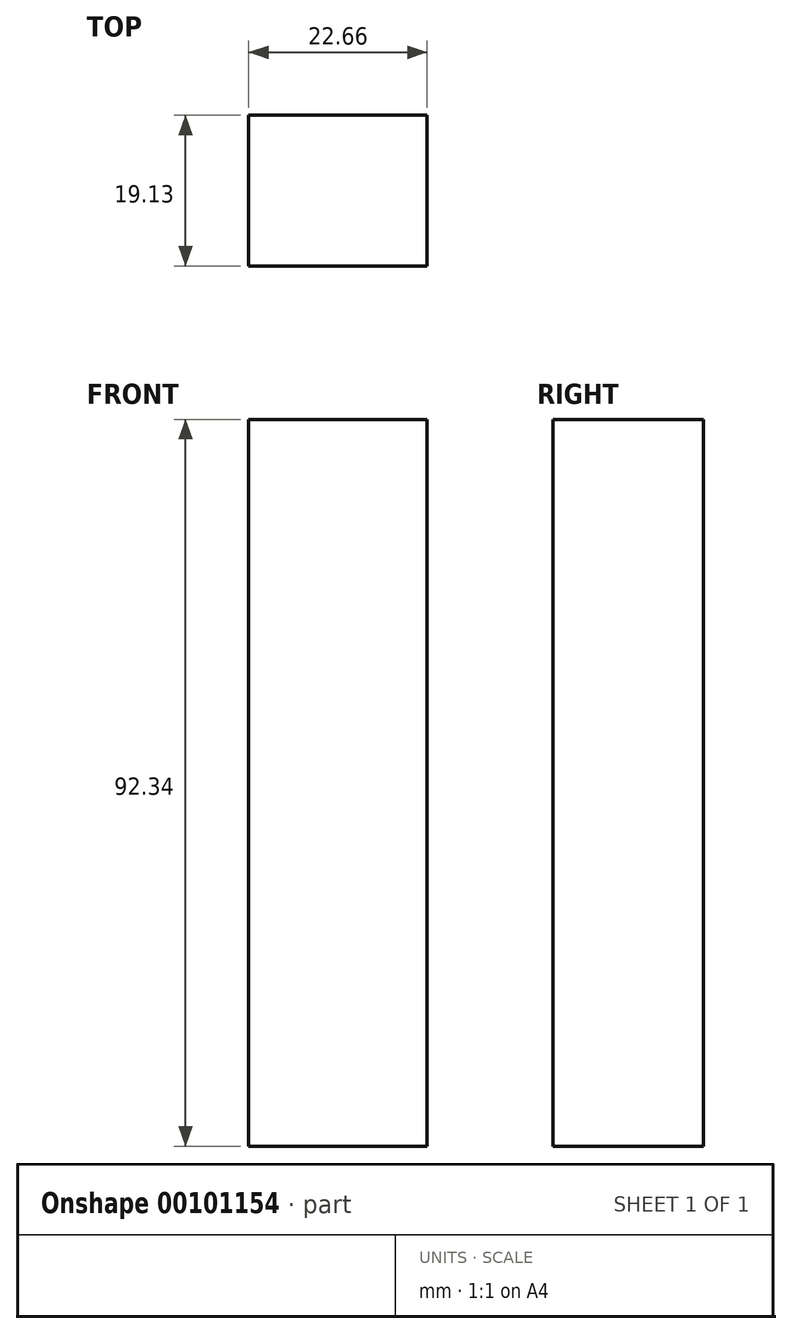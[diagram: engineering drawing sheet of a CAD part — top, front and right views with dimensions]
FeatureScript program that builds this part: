
annotation { "Feature Type Name" : "Feature", "Feature Type Description" : "" }
export const myFeature = defineFeature(function(context is Context, id is Id, definition is map)
    precondition{}
    {
        {
            var Q0;
            Q0=qCreatedBy(makeId("Front.planeOp"),FACE);
            var sketch = newSketch(context, id + "F0", { "sketchPlane" : qUnion([Q0])});
            skLineSegment(sketch, "E0.bottom", {"start": v(11.33, -46.17) * mm, "end": v(-11.33, -46.17) * mm});
            skLineSegment(sketch, "E0.top", {"start": v(11.33, 46.17) * mm, "end": v(-11.33, 46.17) * mm});
            skLineSegment(sketch, "E0.left", {"start": v(11.33, -46.17) * mm, "end": v(11.33, 46.17) * mm});
            skLineSegment(sketch, "E0.right", {"start": v(-11.33, -46.17) * mm, "end": v(-11.33, 46.17) * mm});
            skPoint(sketch, "E0.middle", {"position": v(0, 0) * mm});
            skSolve(sketch);
        }
        {
            var Q0;
            Q0=makeQuery(id+"F0.imprint","IMPRINT",FACE,{"disambiguationData":[TD([[makeQuery(id+"F0.imprint","IMPRINT",EDGE,{"derivedFrom":sQuery(id+"F0.wireOp",EDGE,"E0.bottom")}),-1.0]])]});
            extrude(context, id + "F1", {"entities" : qUnion([Q0]), "oppositeDirection" : true, "depth" : 19.13 * mm});
        }
    });
